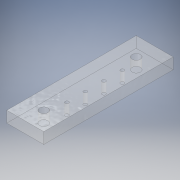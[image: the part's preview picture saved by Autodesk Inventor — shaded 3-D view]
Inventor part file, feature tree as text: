
AUTODESK INVENTOR PART (.ipt)
format: ipt  version: 2019 (Build 230136000, 136)  size: 129,536 bytes
history: native  units: mm
features: extrude x1, sketch x1
ambient origin geometry x8: Origin, YZ Plane, XZ Plane, XY Plane, X Axis, Y Axis, Z Axis, Center Point
bodies: Body1 (feature_tree)
feature tree (2):
  extrude  "Extrusion2"  Depth=20.0mm
  sketch  "Sketch2"  dims[d31=6.0mm d32=0.0mm d76=20.0mm d78=10.0mm d79=50.0mm d80=10.0mm d81=4.5mm d82=10.0mm d83=1.9mm d84=40.0mm d86=10.0mm d87=10.0mm d89=10.0mm d91=10.0mm d92=7.5mm]
